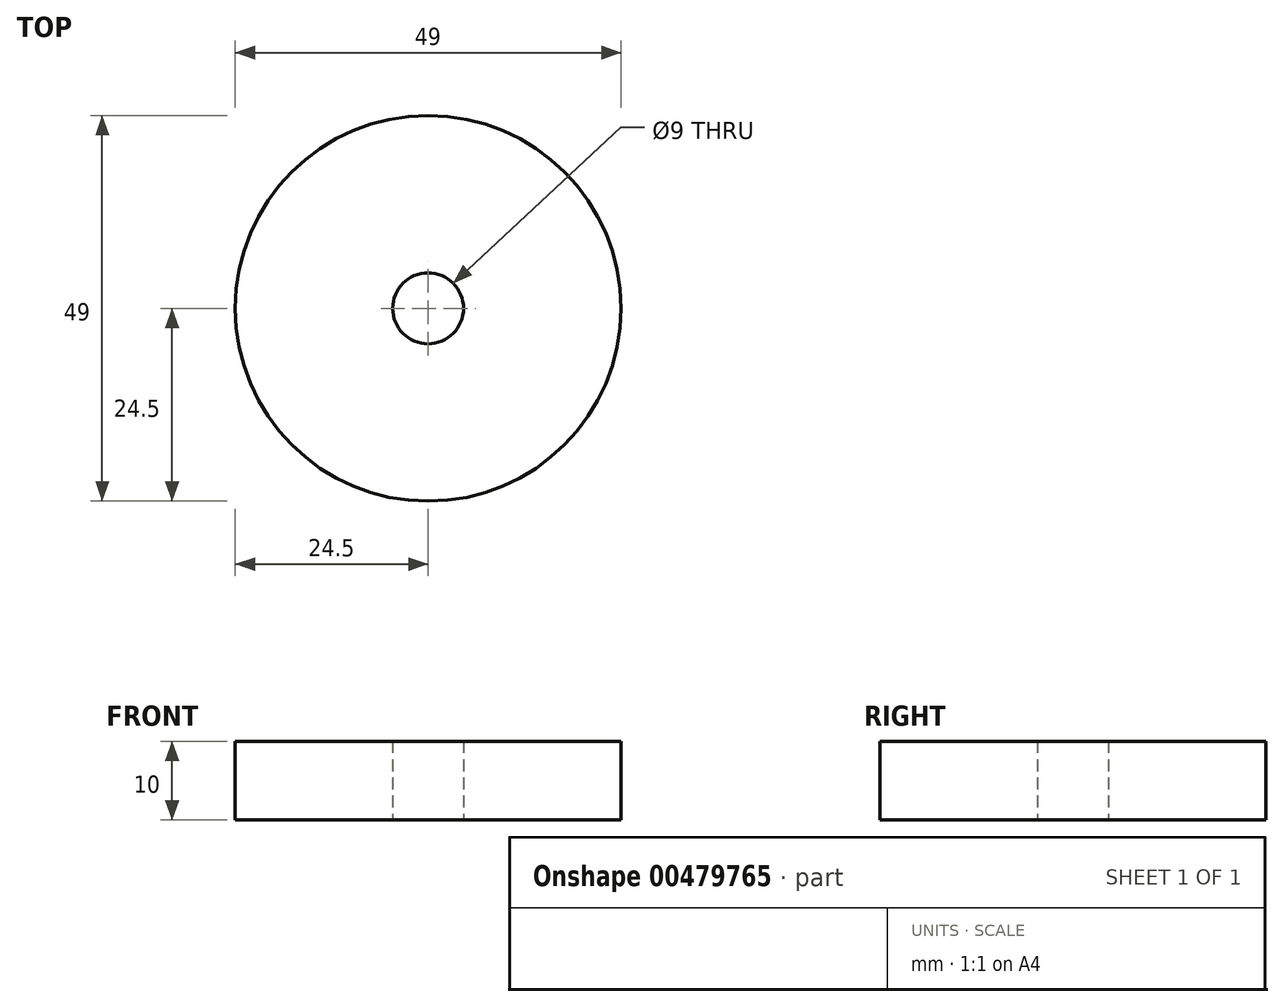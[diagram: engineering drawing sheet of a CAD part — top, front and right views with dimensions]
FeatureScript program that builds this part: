
annotation { "Feature Type Name" : "Feature", "Feature Type Description" : "" }
export const myFeature = defineFeature(function(context is Context, id is Id, definition is map)
    precondition{}
    {
        {
            var Q0;
            Q0=qCreatedBy(makeId("Top.planeOp"),FACE);
            var sketch = newSketch(context, id + "F0", { "sketchPlane" : qUnion([Q0])});
            skCircle(sketch, "E0", {"center": v(0, 0) * mm, "radius": 24.5 * mm});
            skCircle(sketch, "E1", {"center": v(0, 0) * mm, "radius": 4.5 * mm});
            skSolve(sketch);
        }
        {
            var Q0;
            Q0=makeQuery(id+"F0.imprint","IMPRINT",FACE,{"disambiguationData":[TD([[makeQuery(id+"F0.imprint","IMPRINT",EDGE,{"derivedFrom":sQuery(id+"F0.wireOp",EDGE,"E0")}),1.0]])]});
            extrude(context, id + "F1", {"entities" : qUnion([Q0]), "depth" : 10 * mm});
        }
    });
